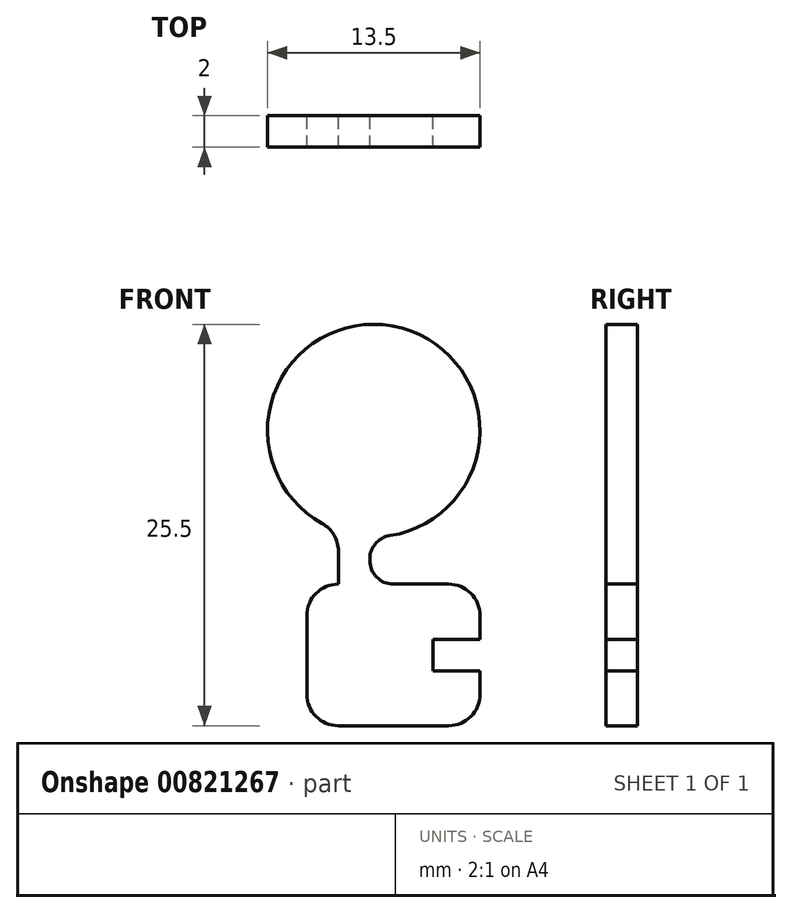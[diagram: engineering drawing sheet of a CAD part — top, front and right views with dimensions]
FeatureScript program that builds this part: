
annotation { "Feature Type Name" : "Feature", "Feature Type Description" : "" }
export const myFeature = defineFeature(function(context is Context, id is Id, definition is map)
    precondition{}
    {
        {
            var Q0;
            Q0=qCreatedBy(makeId("Front.planeOp"),FACE);
            var sketch = newSketch(context, id + "F0", { "sketchPlane" : qUnion([Q0])});
            skArc(sketch, "E0", {"start": v(1.02, -6.67) * mm, "mid": v(1.2, 6.64) * mm, "end": v(-3.28, -5.9) * mm});
            skLineSegment(sketch, "E1", {"start": v(-2.25, -9.75) * mm, "end": v(-2.25, -9.75) * mm});
            skLineSegment(sketch, "E2", {"start": v(-4.25, -11.75) * mm, "end": v(-4.25, -16.75) * mm});
            skLineSegment(sketch, "E3", {"start": v(-2.25, -18.75) * mm, "end": v(4.75, -18.75) * mm});
            skLineSegment(sketch, "E4", {"start": v(6.75, -16.75) * mm, "end": v(6.75, -15.25) * mm});
            skLineSegment(sketch, "E5", {"start": v(-0.25, -8.25) * mm, "end": v(-0.25, -8.15) * mm});
            skLineSegment(sketch, "E6", {"start": v(-2.25, -9.75) * mm, "end": v(-2.25, -7.65) * mm});
            skLineSegment(sketch, "E7.trimOffspring", {"start": v(1.25, -9.75) * mm, "end": v(4.75, -9.75) * mm});
            skLineSegment(sketch, "E8", {"start": v(6.75, -13.25) * mm, "end": v(3.75, -13.25) * mm});
            skLineSegment(sketch, "E9", {"start": v(3.75, -13.25) * mm, "end": v(3.75, -15.25) * mm});
            skLineSegment(sketch, "E10", {"start": v(3.75, -15.25) * mm, "end": v(6.75, -15.25) * mm});
            skPoint(sketch, "E11.end.orphan", {"position": v(3.75, -14.25) * mm});
            skPoint(sketch, "E11.start.orphan", {"position": v(6.75, -14.25) * mm});
            skLineSegment(sketch, "E12.trimOffspring", {"start": v(6.75, -13.25) * mm, "end": v(6.75, -11.75) * mm});
            skPoint(sketch, "E13.visualSharp", {"position": v(-2.25, -6.36) * mm});
            skArc(sketch, "E13.filletArc", {"start": v(-2.25, -7.65) * mm, "mid": v(-2.53, -6.63) * mm, "end": v(-3.28, -5.9) * mm});
            skPoint(sketch, "E14.visualSharp", {"position": v(-0.25, -6.75) * mm});
            skArc(sketch, "E14.filletArc", {"start": v(1.02, -6.67) * mm, "mid": v(0.11, -7.18) * mm, "end": v(-0.25, -8.15) * mm});
            skPoint(sketch, "E15.visualSharp", {"position": v(-0.25, -9.75) * mm});
            skArc(sketch, "E15.filletArc", {"start": v(-0.25, -8.25) * mm, "mid": v(0.19, -9.31) * mm, "end": v(1.25, -9.75) * mm});
            skPoint(sketch, "E16.visualSharp", {"position": v(6.75, -9.75) * mm});
            skArc(sketch, "E16.filletArc", {"start": v(6.75, -11.75) * mm, "mid": v(6.16, -10.34) * mm, "end": v(4.75, -9.75) * mm});
            skPoint(sketch, "E17.visualSharp", {"position": v(-4.25, -9.75) * mm});
            skArc(sketch, "E17.filletArc", {"start": v(-2.25, -9.75) * mm, "mid": v(-3.66, -10.34) * mm, "end": v(-4.25, -11.75) * mm});
            skPoint(sketch, "E18.visualSharp", {"position": v(-4.25, -18.75) * mm});
            skArc(sketch, "E18.filletArc", {"start": v(-4.25, -16.75) * mm, "mid": v(-3.66, -18.16) * mm, "end": v(-2.25, -18.75) * mm});
            skPoint(sketch, "E19.visualSharp", {"position": v(6.75, -18.75) * mm});
            skArc(sketch, "E19.filletArc", {"start": v(4.75, -18.75) * mm, "mid": v(6.16, -18.16) * mm, "end": v(6.75, -16.75) * mm});
            skSolve(sketch);
        }
        {
            var Q0;
            Q0 = qSketchRegion(id + "F0", true);
            extrude(context, id + "F1", {"entities" : qUnion([Q0]), "depth" : 2 * mm, "offsetDistance" : 25 * mm});
        }
    });
